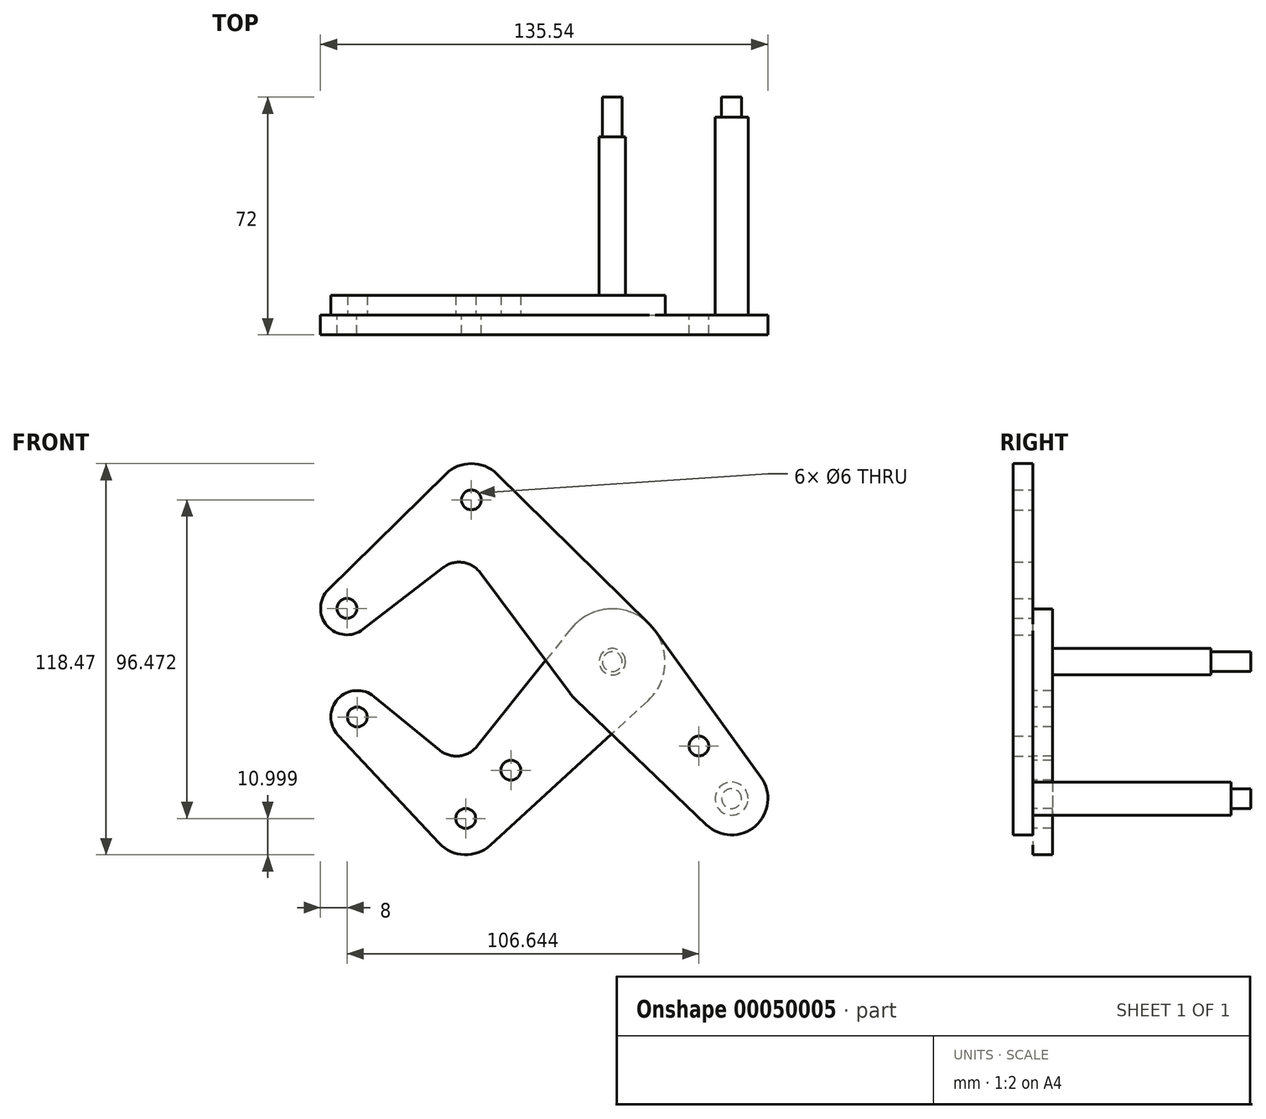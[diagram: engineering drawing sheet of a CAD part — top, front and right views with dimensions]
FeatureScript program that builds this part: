
annotation { "Feature Type Name" : "Feature", "Feature Type Description" : "" }
export const myFeature = defineFeature(function(context is Context, id is Id, definition is map)
    precondition{}
    {
        {
            var Q0;
            Q0=qCreatedBy(makeId("Front.planeOp"),FACE);
            cPlane(context, id + "F0", {"entities" : qUnion([Q0]), "cplaneType" : CPlaneType.OFFSET, "offset" : 30 * mm, "width" : 150 * mm, "height" : 150 * mm});
        }
        {
            var Q0;
            Q0=qCreatedBy(id+"F0.planeOp",FACE);
            var sketch = newSketch(context, id + "F1", { "sketchPlane" : qUnion([Q0])});
            skLineSegment(sketch, "E0", {"start": v(-42.7, 49) * mm, "end": v(36.14, -41.46) * mm, "construction": true});
            skCircle(sketch, "E1", {"center": v(0, 0) * mm, "radius": 3 * mm});
            skCircle(sketch, "E2", {"center": v(36.14, -41.46) * mm, "radius": 3 * mm});
            skCircle(sketch, "E3", {"center": v(-42.7, 49) * mm, "radius": 3 * mm});
            skCircle(sketch, "E4", {"center": v(-80.4, 16.15) * mm, "radius": 3 * mm});
            skLineSegment(sketch, "E5", {"start": v(-42.7, 49) * mm, "end": v(-80.4, 16.15) * mm, "construction": true});
            skCircle(sketch, "E6", {"center": v(36.14, -41.46) * mm, "radius": 11 * mm});
            skCircle(sketch, "E7", {"center": v(-80.4, 16.15) * mm, "radius": 8 * mm});
            skCircle(sketch, "E8", {"center": v(-42.7, 49) * mm, "radius": 11 * mm});
            skLineSegment(sketch, "E9", {"start": v(-86, 21.85) * mm, "end": v(-50.42, 56.84) * mm});
            skLineSegment(sketch, "E10", {"start": v(-75.52, 9.81) * mm, "end": v(-51.3, 28.49) * mm});
            skCircle(sketch, "E11", {"center": v(0, 0) * mm, "radius": 16 * mm});
            skLineSegment(sketch, "E12", {"start": v(-35, 56.84) * mm, "end": v(11.22, 11.4) * mm});
            skLineSegment(sketch, "E13", {"start": v(-40, 26.93) * mm, "end": v(-12.83, -9.55) * mm});
            skLineSegment(sketch, "E14", {"start": v(-11.06, -11.57) * mm, "end": v(28.54, -49.41) * mm});
            skLineSegment(sketch, "E15", {"start": v(12.97, 9.37) * mm, "end": v(45.05, -35.02) * mm});
            skArc(sketch, "E16.filletArc", {"start": v(-40, 26.93) * mm, "mid": v(-45.32, 30.08) * mm, "end": v(-51.3, 28.49) * mm});
            skLineSegment(sketch, "E17", {"start": v(0, 0) * mm, "end": v(-44.4, -47.47) * mm, "construction": true});
            skLineSegment(sketch, "E18", {"start": v(-44.4, -47.47) * mm, "end": v(-77.27, -16.73) * mm, "construction": true});
            skCircle(sketch, "E19", {"center": v(-77.27, -16.73) * mm, "radius": 3 * mm});
            skCircle(sketch, "E20", {"center": v(-44.4, -47.47) * mm, "radius": 3 * mm});
            skCircle(sketch, "E21", {"center": v(-77.27, -16.73) * mm, "radius": 8 * mm});
            skCircle(sketch, "E22", {"center": v(-44.4, -47.47) * mm, "radius": 11 * mm});
            skLineSegment(sketch, "E23", {"start": v(-72.2, -10.54) * mm, "end": v(-52.3, -26.8) * mm});
            skLineSegment(sketch, "E24", {"start": v(-83.1, -22.2) * mm, "end": v(-52.43, -54.99) * mm});
            skLineSegment(sketch, "E25", {"start": v(-12.5, 10) * mm, "end": v(-41, -25.61) * mm});
            skLineSegment(sketch, "E26", {"start": v(10.8, -11.8) * mm, "end": v(-36.97, -55.58) * mm});
            skArc(sketch, "E27.filletArc", {"start": v(-52.3, -26.8) * mm, "mid": v(-46.4, -28.57) * mm, "end": v(-41, -25.61) * mm});
            skCircle(sketch, "E28", {"center": v(-30.74, -32.86) * mm, "radius": 3 * mm});
            skCircle(sketch, "E29", {"center": v(26.24, -25.54) * mm, "radius": 3 * mm});
            skLineSegment(sketch, "E30", {"start": v(26.24, -25.54) * mm, "end": v(23.98, -27.52) * mm, "construction": true});
            skCircle(sketch, "E31", {"center": v(0, 0) * mm, "radius": 4 * mm});
            skCircle(sketch, "E32", {"center": v(-80.4, 16.15) * mm, "radius": 5 * mm});
            skCircle(sketch, "E33", {"center": v(-77.27, -16.73) * mm, "radius": 5 * mm});
            skCircle(sketch, "E34", {"center": v(36.14, -41.46) * mm, "radius": 5 * mm});
            skCircle(sketch, "E35", {"center": v(-44.4, -47.47) * mm, "radius": 5 * mm});
            skSolve(sketch);
        }
        {
            var Q0;
            Q0=makeQuery(id+"F1.imprint","IMPRINT",FACE,{"disambiguationData":[TD([[makeQuery(id+"F1.imprint","IMPRINT",EDGE,{"derivedFrom":sQuery(id+"F1.wireOp",EDGE,"E32")}),-1.0]])]});
            var Q1;
            Q1=makeQuery(id+"F1.imprint","IMPRINT",FACE,{"disambiguationData":[TD([[makeQuery(id+"F1.imprint","IMPRINT",EDGE,{"derivedFrom":sQuery(id+"F1.wireOp",EDGE,"E4")}),-1.0]])]});
            var Q2;
            {var subQ9=sQuery(id+"F1.wireOp",EDGE,"E9");Q2=makeQuery(id+"F1.imprint","IMPRINT",FACE,{"disambiguationData":[TD([[makeQuery(id+"F1.imprint","IMPRINT",EDGE,{"derivedFrom":subQ9}),-1.0]])]});}
            var Q3;
            Q3=makeQuery(id+"F1.imprint","IMPRINT",FACE,{"disambiguationData":[TD([[makeQuery(id+"F1.imprint","IMPRINT",EDGE,{"derivedFrom":sQuery(id+"F1.wireOp",EDGE,"E3")}),-1.0]])]});
            var Q4;
            Q4=makeQuery(id+"F1.imprint","IMPRINT",FACE,{"disambiguationData":[TD([[makeQuery(id+"F1.imprint","IMPRINT",EDGE,{"derivedFrom":sQuery(id+"F1.wireOp",EDGE,"E31")}),-1.0]])]});
            var Q5;
            {var subQ1=sQuery(id+"F1.wireOp",EDGE,"E15");Q5=makeQuery(id+"F1.imprint","IMPRINT",FACE,{"disambiguationData":[TD([[makeQuery(id+"F1.imprint","IMPRINT",EDGE,{"derivedFrom":subQ1}),-1.0]])]});}
            var Q6;
            Q6=makeQuery(id+"F1.imprint","IMPRINT",FACE,{"disambiguationData":[TD([[makeQuery(id+"F1.imprint","IMPRINT",EDGE,{"derivedFrom":sQuery(id+"F1.wireOp",EDGE,"E2")}),-1.0]])]});
            var Q7;
            Q7=makeQuery(id+"F1.imprint","IMPRINT",FACE,{"disambiguationData":[TD([[makeQuery(id+"F1.imprint","IMPRINT",EDGE,{"derivedFrom":sQuery(id+"F1.wireOp",EDGE,"E34")}),-1.0]])]});
            var Q8;
            {var subQ1=sQuery(id+"F1.wireOp",EDGE,"E13");var subQ3=sQuery(id+"F1.wireOp",EDGE,"E11");var subQ5=makeQuery(id+"F1.imprint","INTERSECT",VERTEX,{"derivedFrom":[subQ3,subQ1]});Q8=makeQuery(id+"F1.imprint","IMPRINT",FACE,{"disambiguationData":[TD([[makeQuery(id+"F1.imprint","IMPRINT",EDGE,{"disambiguationData":[TD([[subQ5,1.0]])],"derivedFrom":subQ3}),-1.0]])]});}
            var Q9;
            {var subQ1=sQuery(id+"F1.wireOp",EDGE,"E14");var subQ3=sQuery(id+"F1.wireOp",EDGE,"E11");var subQ5=makeQuery(id+"F1.imprint","INTERSECT",VERTEX,{"derivedFrom":[subQ3,subQ1]});Q9=makeQuery(id+"F1.imprint","IMPRINT",FACE,{"disambiguationData":[TD([[makeQuery(id+"F1.imprint","IMPRINT",EDGE,{"disambiguationData":[TD([[subQ5,-1.0]])],"derivedFrom":subQ3}),-1.0]])]});}
            var Q10;
            Q10=makeQuery(id+"F1.imprint","IMPRINT",FACE,{"disambiguationData":[TD([[makeQuery(id+"F1.imprint","IMPRINT",EDGE,{"derivedFrom":sQuery(id+"F1.wireOp",EDGE,"E1")}),-1.0]])]});
            extrude(context, id + "F2", {"entities" : qUnion([Q0, Q1, Q2, Q3, Q4, Q5, Q6, Q7, Q8, Q9, Q10]), "depth" : 6 * mm});
        }
        {
            var Q0;
            Q0=makeQuery(id+"F1.imprint","IMPRINT",FACE,{"disambiguationData":[TD([[makeQuery(id+"F1.imprint","IMPRINT",EDGE,{"derivedFrom":sQuery(id+"F1.wireOp",EDGE,"E19")}),-1.0]])]});
            var Q1;
            Q1=makeQuery(id+"F1.imprint","IMPRINT",FACE,{"disambiguationData":[TD([[makeQuery(id+"F1.imprint","IMPRINT",EDGE,{"derivedFrom":sQuery(id+"F1.wireOp",EDGE,"E33")}),-1.0]])]});
            var Q2;
            Q2=makeQuery(id+"F1.imprint","IMPRINT",FACE,{"disambiguationData":[TD([[makeQuery(id+"F1.imprint","IMPRINT",EDGE,{"derivedFrom":sQuery(id+"F1.wireOp",EDGE,"E1")}),-1.0]])]});
            var Q3;
            Q3=makeQuery(id+"F1.imprint","IMPRINT",FACE,{"disambiguationData":[TD([[makeQuery(id+"F1.imprint","IMPRINT",EDGE,{"derivedFrom":sQuery(id+"F1.wireOp",EDGE,"E31")}),-1.0]])]});
            var Q4;
            {var subQ1=sQuery(id+"F1.wireOp",EDGE,"E13");var subQ3=sQuery(id+"F1.wireOp",EDGE,"E11");var subQ5=makeQuery(id+"F1.imprint","INTERSECT",VERTEX,{"derivedFrom":[subQ3,subQ1]});Q4=makeQuery(id+"F1.imprint","IMPRINT",FACE,{"disambiguationData":[TD([[makeQuery(id+"F1.imprint","IMPRINT",EDGE,{"disambiguationData":[TD([[subQ5,1.0]])],"derivedFrom":subQ3}),-1.0]])]});}
            var Q5;
            {var subQ1=sQuery(id+"F1.wireOp",EDGE,"E14");var subQ3=sQuery(id+"F1.wireOp",EDGE,"E11");var subQ5=makeQuery(id+"F1.imprint","INTERSECT",VERTEX,{"derivedFrom":[subQ3,subQ1]});Q5=makeQuery(id+"F1.imprint","IMPRINT",FACE,{"disambiguationData":[TD([[makeQuery(id+"F1.imprint","IMPRINT",EDGE,{"disambiguationData":[TD([[subQ5,-1.0]])],"derivedFrom":subQ3}),-1.0]])]});}
            var Q6;
            Q6=makeQuery(id+"F1.imprint","IMPRINT",FACE,{"disambiguationData":[TD([[makeQuery(id+"F1.imprint","IMPRINT",EDGE,{"derivedFrom":sQuery(id+"F1.wireOp",EDGE,"E20")}),-1.0]])]});
            var Q7;
            Q7=makeQuery(id+"F1.imprint","IMPRINT",FACE,{"disambiguationData":[TD([[makeQuery(id+"F1.imprint","IMPRINT",EDGE,{"derivedFrom":sQuery(id+"F1.wireOp",EDGE,"E35")}),-1.0]])]});
            var Q8;
            {var subQ2=sQuery(id+"F1.wireOp",EDGE,"E23");Q8=makeQuery(id+"F1.imprint","IMPRINT",FACE,{"disambiguationData":[TD([[makeQuery(id+"F1.imprint","IMPRINT",EDGE,{"derivedFrom":subQ2}),-1.0]])]});}
            extrude(context, id + "F3", {"entities" : qUnion([Q0, Q1, Q2, Q3, Q4, Q5, Q6, Q7, Q8]), "oppositeDirection" : true, "depth" : 6 * mm});
        }
        {
            var Q0;
            Q0=makeQuery(id+"F1.imprint","IMPRINT",FACE,{"disambiguationData":[TD([[makeQuery(id+"F1.imprint","IMPRINT",EDGE,{"derivedFrom":sQuery(id+"F1.wireOp",EDGE,"E2")}),1.0]])]});
            var Q1;
            Q1=makeQuery(id+"F1.imprint","IMPRINT",FACE,{"disambiguationData":[TD([[makeQuery(id+"F1.imprint","IMPRINT",EDGE,{"derivedFrom":sQuery(id+"F1.wireOp",EDGE,"E2")}),-1.0]])]});
            var Q2;
            Q2=qCreatedBy(makeId("Front.planeOp"),FACE);
            var Q3;
            Q3=makeQuery(id+"F2.opExtrude","CAP_FACE",FACE,{"disambiguationData":[OSD([sQuery(id+"F1.wireOp",EDGE,"E2"),sQuery(id+"F1.wireOp",EDGE,"E3"),sQuery(id+"F1.wireOp",EDGE,"E4"),sQuery(id+"F1.wireOp",EDGE,"E6"),sQuery(id+"F1.wireOp",EDGE,"E7"),sQuery(id+"F1.wireOp",EDGE,"E8"),sQuery(id+"F1.wireOp",EDGE,"E9"),sQuery(id+"F1.wireOp",EDGE,"E10"),sQuery(id+"F1.wireOp",EDGE,"E11"),sQuery(id+"F1.wireOp",EDGE,"E12"),sQuery(id+"F1.wireOp",EDGE,"E13"),sQuery(id+"F1.wireOp",EDGE,"E14"),sQuery(id+"F1.wireOp",EDGE,"E15"),sQuery(id+"F1.wireOp",EDGE,"E16.filletArc"),sQuery(id+"F1.wireOp",EDGE,"E29"),sQuery(id+"F1.wireOp",EDGE,"E31")])],"isStart":false});
            extrude(context, id + "F4", {"entities" : qUnion([Q0, Q1]), "endBound" : BoundingType.UP_TO_SURFACE, "oppositeDirection" : true, "endBoundEntityFace" : qUnion([Q2]), "depth" : 25 * mm, "hasSecondDirection" : true, "secondDirectionBound" : SecondDirectionBoundingType.UP_TO_SURFACE, "secondDirectionOppositeDirection" : false, "secondDirectionBoundEntityFace" : qUnion([Q3]), "secondDirectionDepth" : 25 * mm});
        }
        {
            var Q0;
            Q0=makeQuery(id+"F1.imprint","IMPRINT",FACE,{"disambiguationData":[TD([[makeQuery(id+"F1.imprint","IMPRINT",EDGE,{"derivedFrom":sQuery(id+"F1.wireOp",EDGE,"E1")}),-1.0]])]});
            var Q1;
            Q1=makeQuery(id+"F1.imprint","IMPRINT",FACE,{"disambiguationData":[TD([[makeQuery(id+"F1.imprint","IMPRINT",EDGE,{"derivedFrom":sQuery(id+"F1.wireOp",EDGE,"E1")}),1.0]])]});
            var Q2;
            Q2=qCreatedBy(makeId("Front.planeOp"),FACE);
            var Q3;
            Q3=makeQuery(id+"F2.opExtrude","CAP_FACE",FACE,{"disambiguationData":[OSD([sQuery(id+"F1.wireOp",EDGE,"E2"),sQuery(id+"F1.wireOp",EDGE,"E3"),sQuery(id+"F1.wireOp",EDGE,"E4"),sQuery(id+"F1.wireOp",EDGE,"E6"),sQuery(id+"F1.wireOp",EDGE,"E7"),sQuery(id+"F1.wireOp",EDGE,"E8"),sQuery(id+"F1.wireOp",EDGE,"E9"),sQuery(id+"F1.wireOp",EDGE,"E10"),sQuery(id+"F1.wireOp",EDGE,"E11"),sQuery(id+"F1.wireOp",EDGE,"E12"),sQuery(id+"F1.wireOp",EDGE,"E13"),sQuery(id+"F1.wireOp",EDGE,"E14"),sQuery(id+"F1.wireOp",EDGE,"E15"),sQuery(id+"F1.wireOp",EDGE,"E16.filletArc"),sQuery(id+"F1.wireOp",EDGE,"E29"),sQuery(id+"F1.wireOp",EDGE,"E31")])],"isStart":false});
            extrude(context, id + "F5", {"entities" : qUnion([Q0, Q1]), "endBound" : BoundingType.UP_TO_SURFACE, "oppositeDirection" : true, "endBoundEntityFace" : qUnion([Q2]), "depth" : 25 * mm, "hasSecondDirection" : true, "secondDirectionBound" : SecondDirectionBoundingType.UP_TO_SURFACE, "secondDirectionOppositeDirection" : false, "secondDirectionBoundEntityFace" : qUnion([Q3]), "secondDirectionDepth" : 25 * mm});
        }
        {
            var Q0;
            Q0=makeQuery(id+"F2.opExtrude","SWEPT_BODY",BODY,{"disambiguationData":[OSD([sQuery(id+"F1.wireOp",EDGE,"E2"),sQuery(id+"F1.wireOp",EDGE,"E3"),sQuery(id+"F1.wireOp",EDGE,"E4"),sQuery(id+"F1.wireOp",EDGE,"E6"),sQuery(id+"F1.wireOp",EDGE,"E7"),sQuery(id+"F1.wireOp",EDGE,"E8"),sQuery(id+"F1.wireOp",EDGE,"E9"),sQuery(id+"F1.wireOp",EDGE,"E10"),sQuery(id+"F1.wireOp",EDGE,"E11"),sQuery(id+"F1.wireOp",EDGE,"E12"),sQuery(id+"F1.wireOp",EDGE,"E13"),sQuery(id+"F1.wireOp",EDGE,"E14"),sQuery(id+"F1.wireOp",EDGE,"E15"),sQuery(id+"F1.wireOp",EDGE,"E16.filletArc"),sQuery(id+"F1.wireOp",EDGE,"E29"),sQuery(id+"F1.wireOp",EDGE,"E31")])]});
            var Q1;
            Q1=makeQuery(id+"F3.opExtrude","SWEPT_BODY",BODY,{"disambiguationData":[OSD([sQuery(id+"F1.wireOp",EDGE,"E1"),sQuery(id+"F1.wireOp",EDGE,"E11"),sQuery(id+"F1.wireOp",EDGE,"E19"),sQuery(id+"F1.wireOp",EDGE,"E20"),sQuery(id+"F1.wireOp",EDGE,"E21"),sQuery(id+"F1.wireOp",EDGE,"E22"),sQuery(id+"F1.wireOp",EDGE,"E23"),sQuery(id+"F1.wireOp",EDGE,"E24"),sQuery(id+"F1.wireOp",EDGE,"E25"),sQuery(id+"F1.wireOp",EDGE,"E26"),sQuery(id+"F1.wireOp",EDGE,"E27.filletArc"),sQuery(id+"F1.wireOp",EDGE,"E28")])]});
            var Q2;
            Q2=makeQuery(id+"F5.opExtrude","SWEPT_BODY",BODY,{"disambiguationData":[OSD([sQuery(id+"F1.wireOp",EDGE,"E1"),sQuery(id+"F1.wireOp",EDGE,"E11")])]});
            var Q3;
            Q3=makeQuery(id+"F4.opExtrude","SWEPT_BODY",BODY,{"disambiguationData":[OSD([sQuery(id+"F1.wireOp",EDGE,"E34")])]});
            booleanBodies(context, id + "F6", {"operationType" : BooleanOperationType.SUBTRACTION, "tools" : qUnion([Q0, Q1]), "targets" : qUnion([Q2, Q3]), "keepTools" : true});
        }
        {
            var Q0;
            Q0=makeQuery(id+"F3.opExtrude","SWEPT_BODY",BODY,{"disambiguationData":[OSD([sQuery(id+"F1.wireOp",EDGE,"E1"),sQuery(id+"F1.wireOp",EDGE,"E11"),sQuery(id+"F1.wireOp",EDGE,"E19"),sQuery(id+"F1.wireOp",EDGE,"E20"),sQuery(id+"F1.wireOp",EDGE,"E21"),sQuery(id+"F1.wireOp",EDGE,"E22"),sQuery(id+"F1.wireOp",EDGE,"E23"),sQuery(id+"F1.wireOp",EDGE,"E24"),sQuery(id+"F1.wireOp",EDGE,"E25"),sQuery(id+"F1.wireOp",EDGE,"E26"),sQuery(id+"F1.wireOp",EDGE,"E27.filletArc"),sQuery(id+"F1.wireOp",EDGE,"E28")])]});
            var Q1;
            Q1=makeQuery(id+"F2.opExtrude","SWEPT_BODY",BODY,{"disambiguationData":[OSD([sQuery(id+"F1.wireOp",EDGE,"E1"),sQuery(id+"F1.wireOp",EDGE,"E2"),sQuery(id+"F1.wireOp",EDGE,"E3"),sQuery(id+"F1.wireOp",EDGE,"E4"),sQuery(id+"F1.wireOp",EDGE,"E6"),sQuery(id+"F1.wireOp",EDGE,"E7"),sQuery(id+"F1.wireOp",EDGE,"E8"),sQuery(id+"F1.wireOp",EDGE,"E9"),sQuery(id+"F1.wireOp",EDGE,"E10"),sQuery(id+"F1.wireOp",EDGE,"E11"),sQuery(id+"F1.wireOp",EDGE,"E12"),sQuery(id+"F1.wireOp",EDGE,"E13"),sQuery(id+"F1.wireOp",EDGE,"E14"),sQuery(id+"F1.wireOp",EDGE,"E15"),sQuery(id+"F1.wireOp",EDGE,"E16.filletArc"),sQuery(id+"F1.wireOp",EDGE,"E29")])]});
            var Q2;
            Q2=makeQuery(id+"F5.opExtrude","SWEPT_BODY",BODY,{"disambiguationData":[OSD([sQuery(id+"F1.wireOp",EDGE,"E31")])]});
            booleanBodies(context, id + "F7", {"operationType" : BooleanOperationType.SUBTRACTION, "tools" : qUnion([Q0, Q1]), "targets" : qUnion([Q2]), "keepTools" : true});
        }
        {
            var Q0;
            Q0=makeQuery(id+"F5.opExtrude","SWEPT_BODY",BODY,{"disambiguationData":[OSD([sQuery(id+"F1.wireOp",EDGE,"E31")])]});
            var Q1;
            Q1=qCreatedBy(makeId("Front.planeOp"),FACE);
            mirror(context, id + "F8", {"operationType" : NewBodyOperationType.ADD, "entities" : qUnion([Q0]), "mirrorPlane" : qUnion([Q1])});
        }
        {
            var Q0;
            Q0=makeQuery(id+"F4.opExtrude","SWEPT_BODY",BODY,{"disambiguationData":[OSD([sQuery(id+"F1.wireOp",EDGE,"E34")])]});
            var Q1;
            Q1=qCreatedBy(makeId("Front.planeOp"),FACE);
            mirror(context, id + "F9", {"operationType" : NewBodyOperationType.ADD, "entities" : qUnion([Q0]), "mirrorPlane" : qUnion([Q1])});
        }
    });
